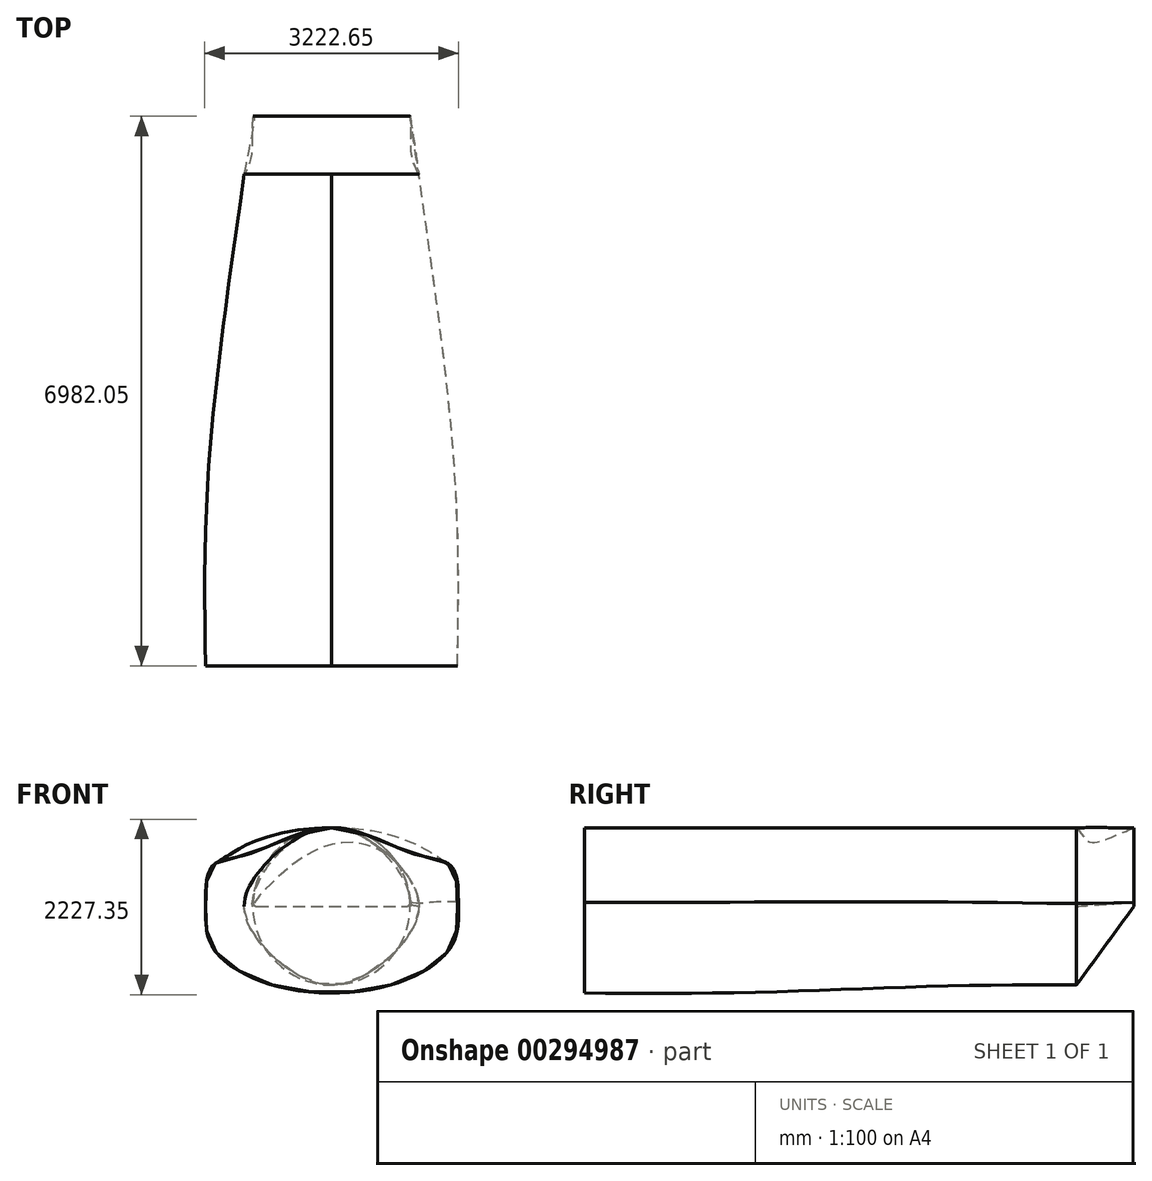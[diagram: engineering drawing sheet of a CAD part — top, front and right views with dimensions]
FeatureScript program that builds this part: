
annotation { "Feature Type Name" : "Feature", "Feature Type Description" : "" }
export const myFeature = defineFeature(function(context is Context, id is Id, definition is map)
    precondition{}
    {
        {
            var Q0;
            Q0=qCreatedBy(makeId("Front.planeOp"),FACE);
            cPlane(context, id + "F0", {"entities" : qUnion([Q0]), "cplaneType" : CPlaneType.OFFSET, "offset" : 1750 * mm, "width" : 150 * mm, "height" : 150 * mm});
        }
        {
            var Q0;
            Q0=qCreatedBy(id+"F0.planeOp",FACE);
            var sketch = newSketch(context, id + "F1", { "sketchPlane" : qUnion([Q0])});
            skPoint(sketch, "E0.middle", {"position": v(0, 0) * mm});
            skFitSpline(sketch, "E1", {"points": [v(0, 1000) * mm, v(1060, 662.5) * mm, v(1517.6, 506.84) * mm, v(1600, 0) * mm, v(1517.6, -506.84) * mm, v(750, -1000) * mm, v(-750, -1000) * mm, v(-1517.6, -506.84) * mm, v(-1600, 0) * mm, v(-1517.6, 506.84) * mm, v(-1060, 662.5) * mm, v(0, 1000) * mm]});
            skSolve(sketch);
        }
        {
            var Q0;
            Q0=qCreatedBy(makeId("Front.planeOp"),FACE);
            var sketch = newSketch(context, id + "F2", { "sketchPlane" : qUnion([Q0])});
            skPoint(sketch, "E2.middle", {"position": v(0, 0) * mm});
            skFitSpline(sketch, "E3", {"points": [v(0, 1000) * mm, v(1060, 662.5) * mm, v(1517.6, 506.84) * mm, v(1600, 0) * mm, v(1517.6, -506.84) * mm, v(750, -1000) * mm, v(-750, -1000) * mm, v(-1517.6, -506.84) * mm, v(-1600, 0) * mm, v(-1517.6, 506.84) * mm, v(-1060, 662.5) * mm, v(0, 1000) * mm]});
            skSolve(sketch);
        }
        {
            var Q0;
            Q0=qCreatedBy(makeId("Front.planeOp"),FACE);
            cPlane(context, id + "F3", {"entities" : qUnion([Q0]), "cplaneType" : CPlaneType.OFFSET, "offset" : 3500 * mm, "oppositeDirection" : true, "width" : 150 * mm, "height" : 150 * mm});
        }
        {
            var Q0;
            Q0=qCreatedBy(id+"F3.planeOp",FACE);
            var sketch = newSketch(context, id + "F4", { "sketchPlane" : qUnion([Q0])});
            skPoint(sketch, "E4.middle", {"position": v(0, 0) * mm});
            skFitSpline(sketch, "E5", {"points": [v(0, 1000) * mm, v(1060, 662.5) * mm, v(1250, 0) * mm, v(1060, -662.5) * mm, v(0, -1000) * mm, v(-1060, -662.5) * mm, v(-1250, 0) * mm, v(-1060, 662.5) * mm, v(0, 1000) * mm]});
            skSolve(sketch);
        }
        {
            var Q0;
            Q0=qCreatedBy(makeId("Front.planeOp"),FACE);
            cPlane(context, id + "F5", {"entities" : qUnion([Q0]), "cplaneType" : CPlaneType.OFFSET, "offset" : 4500 * mm, "oppositeDirection" : true, "width" : 150 * mm, "height" : 150 * mm});
        }
        {
            var Q0;
            Q0=qCreatedBy(id+"F5.planeOp",FACE);
            var sketch = newSketch(context, id + "F6", { "sketchPlane" : qUnion([Q0])});
            skPoint(sketch, "E6.middle", {"position": v(0, 0) * mm});
            skFitSpline(sketch, "E7", {"points": [v(0, 1000) * mm, v(848, 530) * mm, v(1108.5, 0) * mm, v(848, -530) * mm, v(0, -1000) * mm, v(-848, -530) * mm, v(-1108.5, 0) * mm, v(-848, 530) * mm, v(0, 1000) * mm]});
            skSolve(sketch);
        }
        {
            var Q0;
            Q0=makeQuery(id+"F1.imprint","IMPRINT",FACE,{"disambiguationData":[TD([[makeQuery(id+"F1.imprint","IMPRINT",EDGE,{"derivedFrom":sQuery(id+"F1.wireOp",EDGE,"E1")}),-1.0]])]});
            var Q1;
            Q1=makeQuery(id+"F2.imprint","IMPRINT",FACE,{"disambiguationData":[TD([[makeQuery(id+"F2.imprint","IMPRINT",EDGE,{"derivedFrom":sQuery(id+"F2.wireOp",EDGE,"E3")}),-1.0]])]});
            var Q2;
            Q2=makeQuery(id+"F4.imprint","IMPRINT",FACE,{"disambiguationData":[TD([[makeQuery(id+"F4.imprint","IMPRINT",EDGE,{"derivedFrom":sQuery(id+"F4.wireOp",EDGE,"E5")}),-1.0]])]});
            var Q3;
            Q3=makeQuery(id+"F6.imprint","IMPRINT",FACE,{"disambiguationData":[TD([[makeQuery(id+"F6.imprint","IMPRINT",EDGE,{"derivedFrom":sQuery(id+"F6.wireOp",EDGE,"E7")}),-1.0]])]});
            loft(context, id + "F7", {"sheetProfilesArray" : [{ "sheetProfileEntities" : qUnion([Q0]) }, { "sheetProfileEntities" : qUnion([Q1]) }, { "sheetProfileEntities" : qUnion([Q2]) }, { "sheetProfileEntities" : qUnion([Q3]) }]});
        }
        {
            var Q0;
            Q0=qCreatedBy(makeId("Front.planeOp"),FACE);
            cPlane(context, id + "F8", {"entities" : qUnion([Q0]), "cplaneType" : CPlaneType.OFFSET, "offset" : 5232.05 * mm, "oppositeDirection" : true, "width" : 150 * mm, "height" : 150 * mm});
        }
        {
            var Q0;
            Q0=qCreatedBy(id+"F8.planeOp",FACE);
            var sketch = newSketch(context, id + "F9", { "sketchPlane" : qUnion([Q0])});
            skArc(sketch, "E8", {"start": v(998.61, 52.63) * mm, "mid": v(0, 1000) * mm, "end": v(-998.61, 52.63) * mm});
            skLineSegment(sketch, "E9", {"start": v(-948.68, 0) * mm, "end": v(948.68, 0) * mm});
            skArc(sketch, "E10.filletArc", {"start": v(-998.61, 52.63) * mm, "mid": v(-984.96, 15.59) * mm, "end": v(-948.68, 0) * mm});
            skArc(sketch, "E11.filletArc", {"start": v(948.68, 0) * mm, "mid": v(984.96, 15.59) * mm, "end": v(998.61, 52.63) * mm});
            skLineSegment(sketch, "E12", {"start": v(-998.61, 52.63) * mm, "end": v(998.61, 52.63) * mm, "construction": true});
            skSolve(sketch);
        }
        {
            var Q0;
            Q0=qSketchRegion(id+"F1",true);
            var Q1;
            Q1=qSketchRegion(id+"F2",true);
            var Q2;
            Q2=qSketchRegion(id+"F4",true);
            var Q3;
            Q3=qSketchRegion(id+"F6",true);
            var Q4;
            Q4=qSketchRegion(id+"F9",true);
            loft(context, id + "F10", {"sheetProfilesArray" : [{ "sheetProfileEntities" : qUnion([Q0]) }, { "sheetProfileEntities" : qUnion([Q1]) }, { "sheetProfileEntities" : qUnion([Q2]) }, { "sheetProfileEntities" : qUnion([Q3]) }, { "sheetProfileEntities" : qUnion([Q4]) }]});
        }
        {
            var Q0;
            Q0=qSketchRegion(id+"F6",true);
            var Q1;
            Q1=qSketchRegion(id+"F9",true);
            loft(context, id + "F11", {"sheetProfilesArray" : [{ "sheetProfileEntities" : qUnion([Q0]) }, { "sheetProfileEntities" : qUnion([Q1]) }]});
        }
        {
            var Q0;
            Q0=qSketchRegion(id+"F6",true);
            var Q1;
            Q1=qSketchRegion(id+"F9",true);
            loft(context, id + "F12", {"sheetProfilesArray" : [{ "sheetProfileEntities" : qUnion([Q0]) }, { "sheetProfileEntities" : qUnion([Q1]) }]});
        }
        {
            var Q0;
            Q0=qSketchRegion(id+"F1",true);
            var Q1;
            Q1=qSketchRegion(id+"F2",true);
            var Q2;
            Q2=qSketchRegion(id+"F4",true);
            var Q3;
            Q3=qSketchRegion(id+"F6",true);
            var Q4;
            Q4=qSketchRegion(id+"F9",true);
            loft(context, id + "F13", {"sheetProfilesArray" : [{ "sheetProfileEntities" : qUnion([Q0]) }, { "sheetProfileEntities" : qUnion([Q1]) }, { "sheetProfileEntities" : qUnion([Q2]) }, { "sheetProfileEntities" : qUnion([Q3]) }, { "sheetProfileEntities" : qUnion([Q4]) }]});
        }
        {
            var Q0;
            Q0=qSketchRegion(id+"F1",true);
            var Q1;
            Q1=qSketchRegion(id+"F2",true);
            var Q2;
            Q2=qSketchRegion(id+"F4",true);
            var Q3;
            Q3=qSketchRegion(id+"F6",true);
            var Q4;
            Q4=qSketchRegion(id+"F9",true);
            loft(context, id + "F14", {"sheetProfilesArray" : [{ "sheetProfileEntities" : qUnion([Q0]) }, { "sheetProfileEntities" : qUnion([Q1]) }, { "sheetProfileEntities" : qUnion([Q2]) }, { "sheetProfileEntities" : qUnion([Q3]) }, { "sheetProfileEntities" : qUnion([Q4]) }]});
        }
        {
            var Q0;
            Q0=qSketchRegion(id+"F6",true);
            var Q1;
            Q1=qSketchRegion(id+"F9",true);
            loft(context, id + "F15", {"sheetProfilesArray" : [{ "sheetProfileEntities" : qUnion([Q0]) }, { "sheetProfileEntities" : qUnion([Q1]) }]});
        }
        {
            var Q0;
            Q0=qCreatedBy(makeId("Front.planeOp"),FACE);
            cPlane(context, id + "F16", {"entities" : qUnion([Q0]), "cplaneType" : CPlaneType.OFFSET, "offset" : 4866.03 * mm, "oppositeDirection" : true, "width" : 150 * mm, "height" : 150 * mm});
        }
        {
            var Q0;
            Q0=qSketchRegion(id+"F6",true);
            var Q1;
            Q1=qSketchRegion(id+"F9",true);
            loft(context, id + "F17", {"sheetProfilesArray" : [{ "sheetProfileEntities" : qUnion([Q0]) }, { "sheetProfileEntities" : qUnion([Q1]) }]});
        }
        {
            var Q0;
            Q0=qSketchRegion(id+"F6",true);
            var Q1;
            Q1=qSketchRegion(id+"F9",true);
            loft(context, id + "F18", {"sheetProfilesArray" : [{ "sheetProfileEntities" : qUnion([Q0]) }, { "sheetProfileEntities" : qUnion([Q1]) }]});
        }
        {
            var Q0;
            Q0=sQuery(id+"F9.wireOp",EDGE,"E9");
            var Q1;
            Q1=sQuery(id+"F6.wireOp",VERTEX,"E7.3.internal");
            cPlane(context, id + "F19", {"entities" : qUnion([Q0, Q1]), "cplaneType" : CPlaneType.LINE_ANGLE, "offset" : 25 * mm, "angle" : 0 * degree, "width" : 150 * mm, "height" : 150 * mm});
        }
        {
            var Q0;
            Q0=sQuery(id+"F9.wireOp",EDGE,"E12");
            var Q1;
            Q1=sQuery(id+"F6.wireOp",VERTEX,"E7.2.internal");
            cPlane(context, id + "F20", {"entities" : qUnion([Q0, Q1]), "cplaneType" : CPlaneType.LINE_ANGLE, "offset" : 25 * mm, "angle" : 0 * degree, "width" : 150 * mm, "height" : 150 * mm});
        }
        {
            var Q0;
            Q0=qCreatedBy(id+"F20.planeOp",FACE);
            var sketch = newSketch(context, id + "F21", { "sketchPlane" : qUnion([Q0])});
            skFitSpline(sketch, "E13", {"points": [v(998.61, -5222.36) * mm, v(1108.5, -4488.41) * mm], "startDerivative": vector(105.37, 736.95) * mm, "endDerivative": vector(477, 750) * mm});
            skFitSpline(sketch, "E14", {"points": [v(-998.61, -5222.36) * mm, v(-1108.5, -4488.41) * mm], "startDerivative": vector(-110.43, 730.93) * mm, "endDerivative": vector(-477, 750) * mm});
            skSolve(sketch);
        }
        {
            var Q0;
            Q0=makeQuery(id+"F6.imprint","IMPRINT",FACE,{"disambiguationData":[TD([[makeQuery(id+"F6.imprint","IMPRINT",EDGE,{"derivedFrom":sQuery(id+"F6.wireOp",EDGE,"E7")}),-1.0]])]});
            var Q1;
            Q1=makeQuery(id+"F9.imprint","IMPRINT",FACE,{"disambiguationData":[TD([[makeQuery(id+"F9.imprint","IMPRINT",EDGE,{"derivedFrom":sQuery(id+"F9.wireOp",EDGE,"E8")}),1.0]])]});
            var Q2;
            Q2=sQuery(id+"F21.wireOp",EDGE,"E13");
            var Q3;
            Q3=sQuery(id+"F21.wireOp",EDGE,"E14");
            loft(context, id + "F22", {"addGuides" : true, "sheetProfilesArray" : [{ "sheetProfileEntities" : qUnion([Q0]) }, { "sheetProfileEntities" : qUnion([Q1]) }], "guidesArray" : [{ "guideEntities" : qUnion([Q2]), "guideDerivativeType" : LoftGuideDerivativeType.DEFAULT, "guideDerivativeMagnitude" : 1 }, { "guideEntities" : qUnion([Q3]), "guideDerivativeType" : LoftGuideDerivativeType.DEFAULT, "guideDerivativeMagnitude" : 1 }]});
        }
    });
